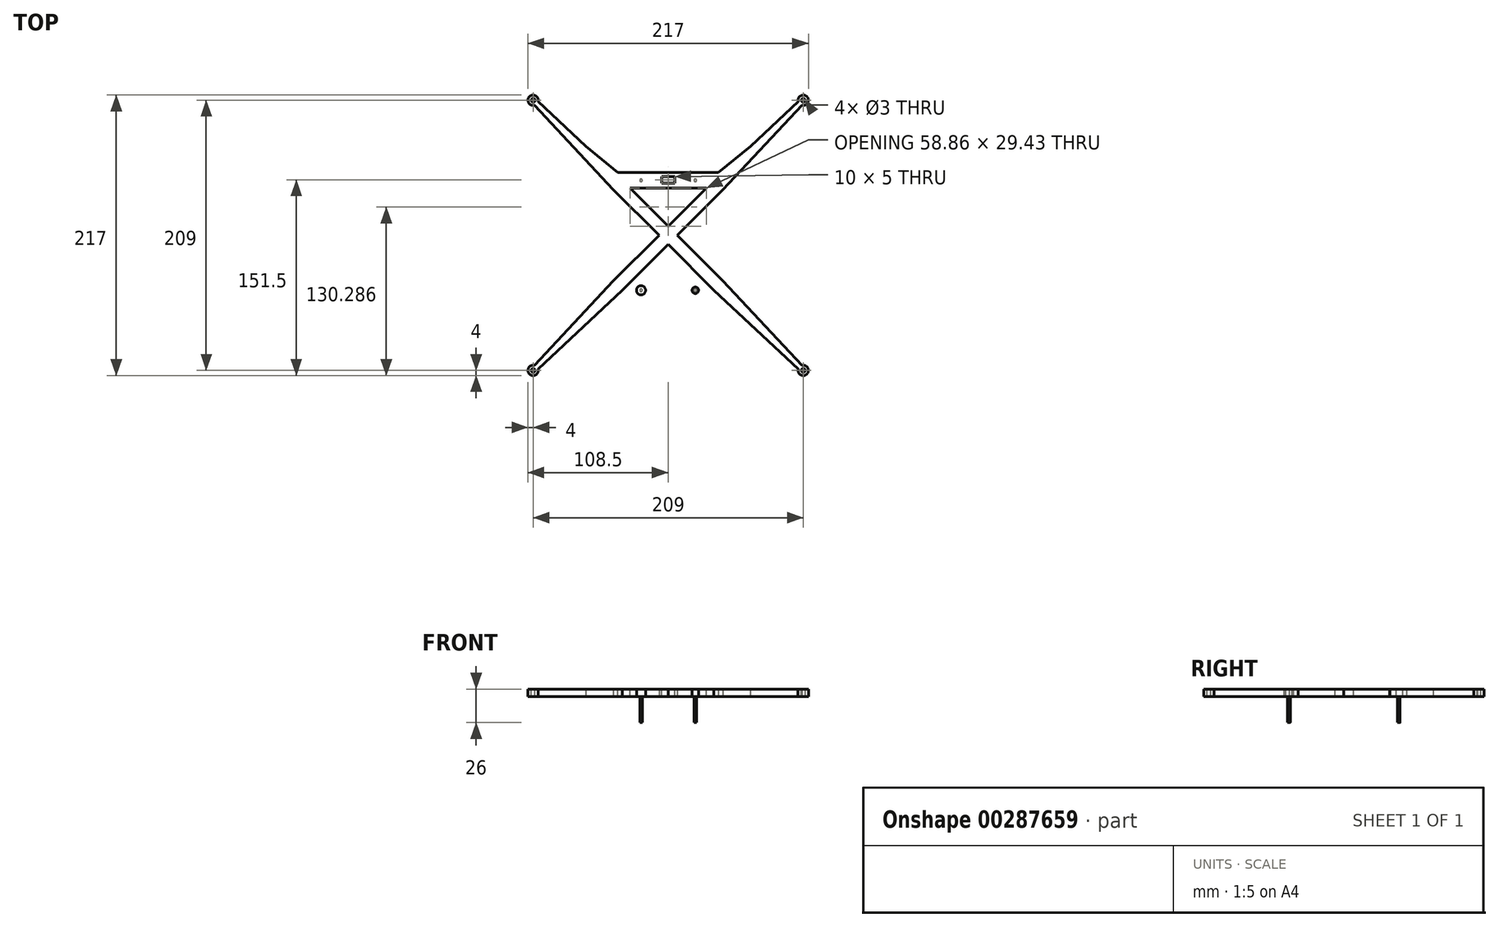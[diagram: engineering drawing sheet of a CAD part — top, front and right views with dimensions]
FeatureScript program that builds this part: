
annotation { "Feature Type Name" : "Feature", "Feature Type Description" : "" }
export const myFeature = defineFeature(function(context is Context, id is Id, definition is map)
    precondition{}
    {
        {
            var Q0;
            Q0=qCreatedBy(makeId("Top.planeOp"),FACE);
            var sketch = newSketch(context, id + "F0", { "sketchPlane" : qUnion([Q0])});
            skCircle(sketch, "E0", {"center": v(-104.5, 104.5) * mm, "radius": 4 * mm});
            skSolve(sketch);
        }
        {
            var Q0;
            Q0=qSketchRegion(id+"F0",true);
            extrude(context, id + "F1", {"entities" : qUnion([Q0]), "depth" : 6 * mm, "offsetDistance" : 25 * mm});
        }
        {
            var Q0;
            Q0=qCreatedBy(makeId("Top.planeOp"),FACE);
            var sketch = newSketch(context, id + "F2", { "sketchPlane" : qUnion([Q0])});
            skLineSegment(sketch, "E1", {"start": v(0, 0) * mm, "end": v(0, 7.07) * mm});
            skLineSegment(sketch, "E2", {"start": v(-100.64, 103.46) * mm, "end": v(-103.46, 100.64) * mm});
            skLineSegment(sketch, "E3", {"start": v(-103.46, 100.64) * mm, "end": v(-42.43, 35.36) * mm});
            skLineSegment(sketch, "E4", {"start": v(-42.43, 35.36) * mm, "end": v(-7.07, 0) * mm});
            skLineSegment(sketch, "E5", {"start": v(-7.07, 0) * mm, "end": v(0, 0) * mm});
            skLineSegment(sketch, "E6", {"start": v(-100.64, 103.46) * mm, "end": v(-35.36, 42.43) * mm});
            skLineSegment(sketch, "E7", {"start": v(-35.36, 42.43) * mm, "end": v(0, 7.07) * mm});
            skLineSegment(sketch, "E8", {"start": v(0, 0) * mm, "end": v(-104.5, 104.5) * mm, "construction": true});
            skSolve(sketch);
        }
        {
            var Q0;
            Q0=qSketchRegion(id+"F2",true);
            var Q1;
            Q1=makeQuery(id+"F1.opExtrude","CAP_FACE",FACE,{"disambiguationData":[OSD([sQuery(id+"F0.wireOp",EDGE,"E0")])],"isStart":false});
            extrude(context, id + "F3", {"entities" : qUnion([Q0]), "operationType" : NewBodyOperationType.ADD, "endBound" : BoundingType.UP_TO_SURFACE, "depth" : 25 * mm, "endBoundEntityFace" : qUnion([Q1]), "offsetDistance" : 25 * mm});
        }
        {
            var Q0;
            {var subQ0=sQuery(id+"F0.wireOp",EDGE,"E0");Q0=makeQuery(id+"F3.boolean.opBoolean","MERGE",FACE,{"derivedFrom":[makeQuery(id+"F1.opExtrude","CAP_FACE",FACE,{"disambiguationData":[OSD([subQ0])],"isStart":false}),makeQuery(id+"F3.opExtrude","CAP_FACE",FACE,{"disambiguationData":[OSD([subQ0])],"isStart":false})]});}
            var sketch = newSketch(context, id + "F4", { "sketchPlane" : qUnion([Q0])});
            skCircle(sketch, "E9", {"center": v(-104.5, 104.5) * mm, "radius": 1.5 * mm});
            skSolve(sketch);
        }
        {
            var Q0;
            Q0=qSketchRegion(id+"F4",true);
            extrude(context, id + "F5", {"entities" : qUnion([Q0]), "operationType" : NewBodyOperationType.REMOVE, "endBound" : BoundingType.THROUGH_ALL, "oppositeDirection" : true, "depth" : 25 * mm, "offsetDistance" : 25 * mm});
        }
        {
            var Q0;
            Q0=makeQuery(id+"F1.opExtrude","SWEPT_BODY",BODY,{"disambiguationData":[OSD([sQuery(id+"F0.wireOp",EDGE,"E0")])]});
            var Q1;
            Q1=makeQuery(id+"F3.opExtrude","SWEPT_EDGE",EDGE,{"disambiguationData":[OSD([sQuery(id+"F2.wireOp",EDGE,"E1"),sQuery(id+"F2.wireOp",EDGE,"E5")])]});
            circularPattern(context, id + "F6", {"entities" : qUnion([Q0]), "axis" : qUnion([Q1]), "angle" : 360 * degree, "instanceCount" : 4, "equalSpace" : true});
        }
        {
            var Q0;
            Q0=makeQuery(id+"F1.opExtrude","SWEPT_BODY",BODY,{"disambiguationData":[OSD([sQuery(id+"F0.wireOp",EDGE,"E0")])]});
            var Q1;
            Q1=makeQuery(id+"F6.opPattern","COPY",BODY,{"derivedFrom":makeQuery(id+"F1.opExtrude","SWEPT_BODY",BODY,{"disambiguationData":[OSD([sQuery(id+"F0.wireOp",EDGE,"E0")])]}),"instanceName":"1"});
            var Q2;
            Q2=makeQuery(id+"F6.opPattern","COPY",BODY,{"derivedFrom":makeQuery(id+"F1.opExtrude","SWEPT_BODY",BODY,{"disambiguationData":[OSD([sQuery(id+"F0.wireOp",EDGE,"E0")])]}),"instanceName":"2"});
            var Q3;
            Q3=makeQuery(id+"F6.opPattern","COPY",BODY,{"derivedFrom":makeQuery(id+"F1.opExtrude","SWEPT_BODY",BODY,{"disambiguationData":[OSD([sQuery(id+"F0.wireOp",EDGE,"E0")])]}),"instanceName":"3"});
            booleanBodies(context, id + "F7", {"operationType" : BooleanOperationType.UNION, "tools" : qUnion([Q0, Q1, Q2, Q3])});
        }
        {
            var Q0;
            Q0=qCreatedBy(makeId("Top.planeOp"),FACE);
            var sketch = newSketch(context, id + "F8", { "sketchPlane" : qUnion([Q0])});
            skLineSegment(sketch, "E10.bottom", {"start": v(-42.5, 36.5) * mm, "end": v(42.5, 36.5) * mm});
            skLineSegment(sketch, "E10.top", {"start": v(-42.5, 48.5) * mm, "end": v(42.5, 48.5) * mm});
            skLineSegment(sketch, "E10.left", {"start": v(-42.5, 36.5) * mm, "end": v(-42.5, 48.5) * mm});
            skLineSegment(sketch, "E10.right", {"start": v(42.5, 36.5) * mm, "end": v(42.5, 48.5) * mm});
            skPoint(sketch, "E10.middle", {"position": v(0, 42.5) * mm});
            skSolve(sketch);
        }
        {
            var Q0;
            Q0=qSketchRegion(id+"F8",true);
            var Q1;
            {var subQ0=sQuery(id+"F0.wireOp",EDGE,"E0");Q1=makeQuery(id+"F3.boolean.opBoolean","MERGE",FACE,{"derivedFrom":[makeQuery(id+"F1.opExtrude","CAP_FACE",FACE,{"disambiguationData":[OSD([subQ0])],"isStart":false}),makeQuery(id+"F3.opExtrude","CAP_FACE",FACE,{"disambiguationData":[OSD([subQ0])],"isStart":false})]});}
            extrude(context, id + "F9", {"entities" : qUnion([Q0]), "operationType" : NewBodyOperationType.ADD, "endBound" : BoundingType.UP_TO_SURFACE, "depth" : 25 * mm, "endBoundEntityFace" : qUnion([Q1]), "offsetDistance" : 25 * mm});
        }
        {
            var Q0;
            {var subQ0=sQuery(id+"F0.wireOp",EDGE,"E0");var subQ1=makeQuery(id+"F3.boolean.opBoolean","MERGE",FACE,{"derivedFrom":[makeQuery(id+"F1.opExtrude","CAP_FACE",FACE,{"disambiguationData":[OSD([subQ0])],"isStart":false}),makeQuery(id+"F3.opExtrude","CAP_FACE",FACE,{"disambiguationData":[OSD([subQ0])],"isStart":false})]});Q0=makeQuery(id+"F9.boolean.opBoolean","MERGE",FACE,{"derivedFrom":[makeQuery(id+"F7.opBoolean","MERGE",FACE,{"derivedFrom":[subQ1,makeQuery(id+"F6.opPattern","COPY",FACE,{"derivedFrom":subQ1,"instanceName":"1"}),makeQuery(id+"F6.opPattern","COPY",FACE,{"derivedFrom":subQ1,"instanceName":"2"}),makeQuery(id+"F6.opPattern","COPY",FACE,{"derivedFrom":subQ1,"instanceName":"3"})]}),makeQuery(id+"F9.opExtrude","CAP_FACE",FACE,{"disambiguationData":[OSD([subQ0])],"isStart":false})]});}
            var sketch = newSketch(context, id + "F10", { "sketchPlane" : qUnion([Q0])});
            skCircle(sketch, "E11", {"center": v(-21, 42.5) * mm, "radius": 3.55 * mm});
            skCircle(sketch, "E12", {"center": v(21, 42.5) * mm, "radius": 2.5 * mm});
            skLineSegment(sketch, "E13.bottom", {"start": v(5, 40.5) * mm, "end": v(-5, 40.5) * mm});
            skLineSegment(sketch, "E13.top", {"start": v(5, 45.5) * mm, "end": v(-5, 45.5) * mm});
            skLineSegment(sketch, "E13.left", {"start": v(5, 40.5) * mm, "end": v(5, 45.5) * mm});
            skLineSegment(sketch, "E13.right", {"start": v(-5, 40.5) * mm, "end": v(-5, 45.5) * mm});
            skPoint(sketch, "E13.middle", {"position": v(0, 43) * mm});
            skSolve(sketch);
        }
        {
            var Q0;
            Q0=qSketchRegion(id+"F10",true);
            extrude(context, id + "F11", {"entities" : qUnion([Q0]), "operationType" : NewBodyOperationType.REMOVE, "endBound" : BoundingType.THROUGH_ALL, "oppositeDirection" : true, "depth" : 25 * mm, "offsetDistance" : 25 * mm});
        }
        {
            var Q0;
            Q0=makeQuery(id+"F9.boolean.opBoolean","INTERSECT",EDGE,{"derivedFrom":[makeQuery(id+"F3.opExtrude","SWEPT_FACE",FACE,{"disambiguationData":[OSD([sQuery(id+"F2.wireOp",EDGE,"E6")])]}),makeQuery(id+"F9.opExtrude","SWEPT_FACE",FACE,{"disambiguationData":[OSD([sQuery(id+"F8.wireOp",EDGE,"E10.top")])]})]});
            var Q1;
            Q1=makeQuery(id+"F9.boolean.opBoolean","INTERSECT",EDGE,{"derivedFrom":[makeQuery(id+"F6.opPattern","COPY",FACE,{"derivedFrom":makeQuery(id+"F3.opExtrude","SWEPT_FACE",FACE,{"disambiguationData":[OSD([sQuery(id+"F2.wireOp",EDGE,"E3")])]}),"instanceName":"1"}),makeQuery(id+"F9.opExtrude","SWEPT_FACE",FACE,{"disambiguationData":[OSD([sQuery(id+"F8.wireOp",EDGE,"E10.top")])]})]});
            chamfer(context, id + "F12", {"entities" : qUnion([Q0, Q1]), "chamferType" : ChamferType.TWO_OFFSETS, "width1" : 3 * mm, "oppositeDirection" : false, "width2" : 30 * mm, "tangentPropagation" : true});
        }
        {
            var Q0;
            Q0=qCreatedBy(makeId("Top.planeOp"),FACE);
            var sketch = newSketch(context, id + "F13", { "sketchPlane" : qUnion([Q0])});
            skCircle(sketch, "E14", {"center": v(-21, 42.5) * mm, "radius": 1 * mm});
            skCircle(sketch, "E15", {"center": v(21, 42.5) * mm, "radius": 1 * mm});
            skCircle(sketch, "E16", {"center": v(-21, -42.5) * mm, "radius": 1 * mm});
            skCircle(sketch, "E17", {"center": v(21, -42.5) * mm, "radius": 1 * mm});
            skSolve(sketch);
        }
        {
            var Q0;
            Q0 = qSketchRegion(id + "F13", true);
            extrude(context, id + "F14", {"entities" : qUnion([Q0]), "oppositeDirection" : true, "depth" : 20 * mm, "offsetDistance" : 25 * mm});
        }
        {
            var Q0;
            {var subQ0=sQuery(id+"F0.wireOp",EDGE,"E0");var subQ1=makeQuery(id+"F3.boolean.opBoolean","MERGE",FACE,{"derivedFrom":[makeQuery(id+"F1.opExtrude","CAP_FACE",FACE,{"disambiguationData":[OSD([subQ0])],"isStart":false}),makeQuery(id+"F3.opExtrude","CAP_FACE",FACE,{"disambiguationData":[OSD([subQ0])],"isStart":false})]});Q0=makeQuery(id+"F7vfmvJLB3VNGqb_1.1.F9.boolean.opBoolean","MERGE",FACE,{"derivedFrom":[makeQuery(id+"F9.boolean.opBoolean","MERGE",FACE,{"derivedFrom":[makeQuery(id+"F7.opBoolean","MERGE",FACE,{"derivedFrom":[subQ1,makeQuery(id+"F6.opPattern","COPY",FACE,{"derivedFrom":subQ1,"instanceName":"1"}),makeQuery(id+"F6.opPattern","COPY",FACE,{"derivedFrom":subQ1,"instanceName":"2"}),makeQuery(id+"F6.opPattern","COPY",FACE,{"derivedFrom":subQ1,"instanceName":"3"})]}),makeQuery(id+"F9.opExtrude","CAP_FACE",FACE,{"disambiguationData":[OSD([subQ0])],"isStart":false})]}),makeQuery(id+"F7vfmvJLB3VNGqb_1.1.F9.opExtrude","CAP_FACE",FACE,{"disambiguationData":[OSD([subQ0])],"isStart":false})]});}
            var sketch = newSketch(context, id + "F15", { "sketchPlane" : qUnion([Q0])});
            skCircle(sketch, "E18.0", {"center": v(-21, -42.5) * mm, "radius": 3.55 * mm});
            skCircle(sketch, "E19.0", {"center": v(21, -42.5) * mm, "radius": 2.5 * mm});
            skCircle(sketch, "E20.0", {"center": v(21, 42.5) * mm, "radius": 2.5 * mm});
            skCircle(sketch, "E21.0", {"center": v(-21, 42.5) * mm, "radius": 3.55 * mm});
            skSolve(sketch);
        }
        {
            var Q0;
            Q0 = qSketchRegion(id + "F15", true);
            extrude(context, id + "F16", {"entities" : qUnion([Q0]), "operationType" : NewBodyOperationType.ADD, "oppositeDirection" : true, "depth" : 6 * mm, "offsetDistance" : 25 * mm});
        }
    });
